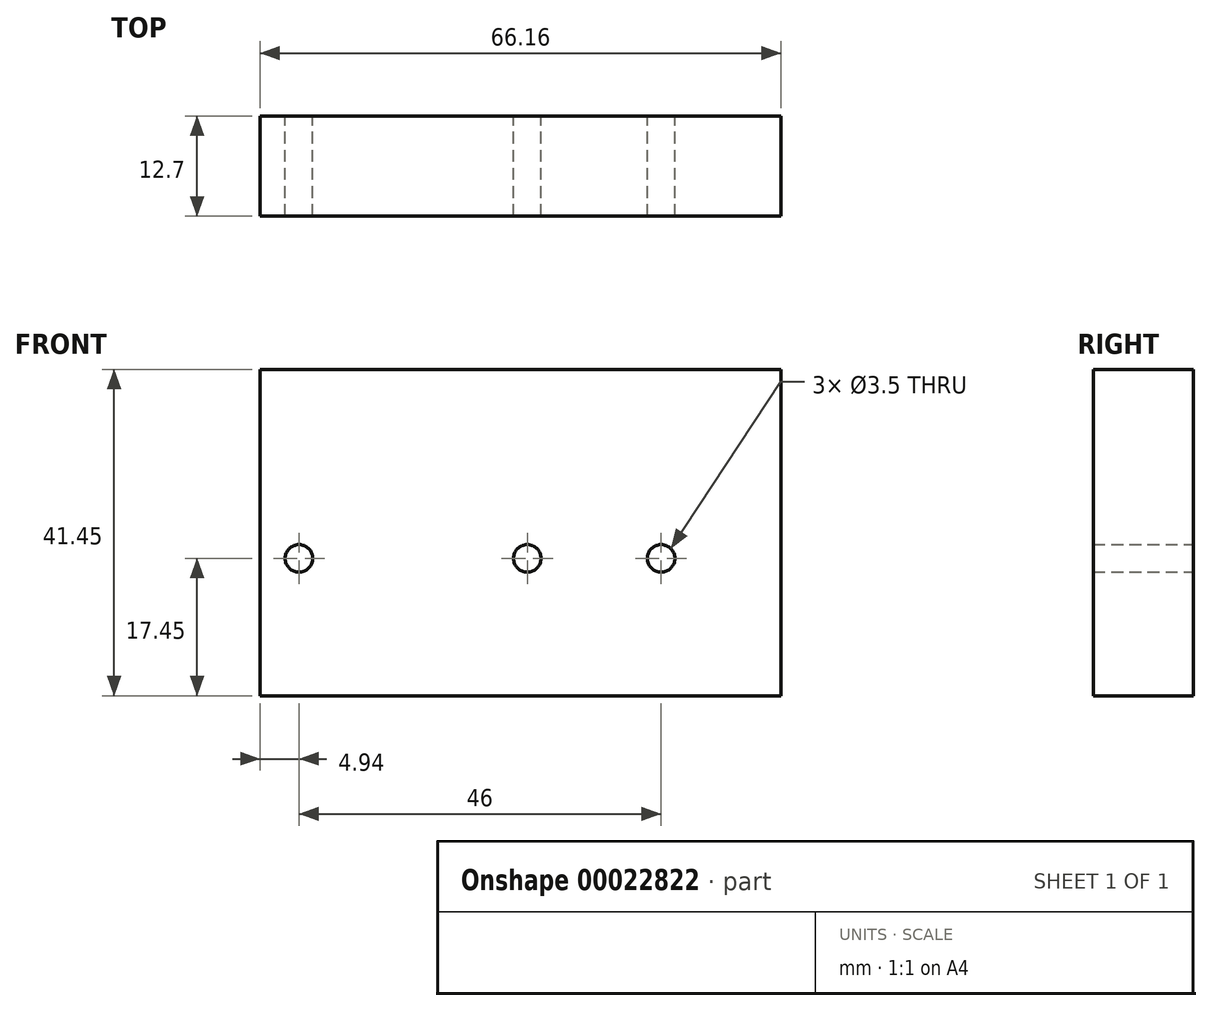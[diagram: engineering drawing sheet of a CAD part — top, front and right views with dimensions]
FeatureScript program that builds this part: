
annotation { "Feature Type Name" : "Feature", "Feature Type Description" : "" }
export const myFeature = defineFeature(function(context is Context, id is Id, definition is map)
    precondition{}
    {
        {
            var Q0;
            Q0=qCreatedBy(makeId("Front.planeOp"),FACE);
            var sketch = newSketch(context, id + "F0", { "sketchPlane" : qUnion([Q0])});
            skLineSegment(sketch, "E0.rect.bottom", {"start": v(-33.08, 24) * mm, "end": v(33.08, 24) * mm});
            skLineSegment(sketch, "E0.rect.top", {"start": v(-33.08, -17.45) * mm, "end": v(33.08, -17.45) * mm});
            skLineSegment(sketch, "E0.rect.left", {"start": v(-33.08, 24) * mm, "end": v(-33.08, -17.45) * mm});
            skLineSegment(sketch, "E0.rect.right", {"start": v(33.08, 24) * mm, "end": v(33.08, -17.45) * mm});
            skPoint(sketch, "E0.rect.middle", {"position": v(0, 3.27) * mm});
            skCircle(sketch, "E1", {"center": v(-28.14, 0) * mm, "radius": 1.75 * mm});
            skLineSegment(sketch, "E2", {"start": v(-28.14, 0) * mm, "end": v(0.86, 0) * mm});
            skLineSegment(sketch, "E3", {"start": v(0.86, 0) * mm, "end": v(17.86, 0) * mm});
            skCircle(sketch, "E4", {"center": v(0.86, 0) * mm, "radius": 1.75 * mm});
            skCircle(sketch, "E5", {"center": v(17.86, 0) * mm, "radius": 1.75 * mm});
            skSolve(sketch);
        }
        {
            var Q0;
            Q0=makeQuery(id+"F0.imprint","IMPRINT",FACE,{"disambiguationData":[TD([[makeQuery(id+"F0.imprint","IMPRINT",EDGE,{"derivedFrom":sQuery(id+"F0.wireOp",EDGE,"E0.rect.bottom")}),-1.0]])]});
            extrude(context, id + "F1", {"entities" : qUnion([Q0]), "depth" : 12.7 * mm});
        }
    });
